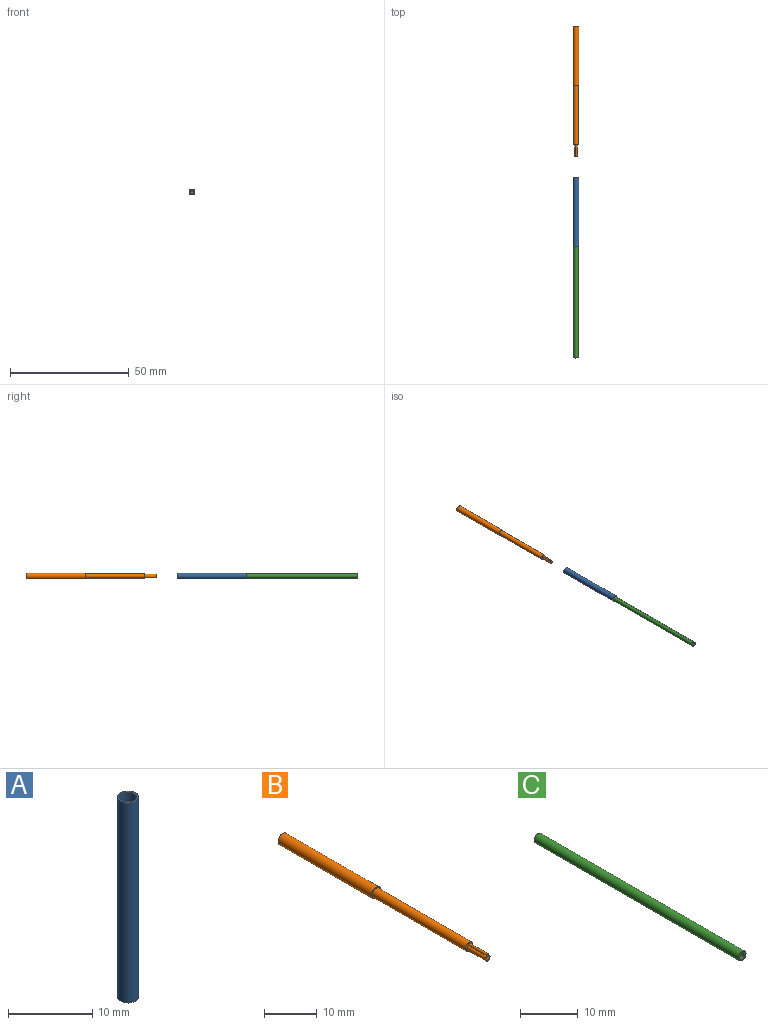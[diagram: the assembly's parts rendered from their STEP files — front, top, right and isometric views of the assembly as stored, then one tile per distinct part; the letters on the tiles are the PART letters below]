
ASSEMBLY  parts=3 mates=1
PART A: 4 faces, bbox 2.5x2.5x29 mm
  f0: cylinder r=1mm len=29mm, axis (0,0,-1), area 182.2mm2, adj f2,f3
  f1: cylinder r=1.25mm len=29mm, axis (0,0,-1), area 227.8mm2, adj f2,f3
  f2: plane 2.5x2.5mm, normal (0,0,1), area 1.8mm2, adj f0,f1
  f3: plane 2.5x2.5mm, normal (0,0,-1), area 1.8mm2, adj f0,f1
PART B: 8 faces, bbox 2.5x55x2.5 mm
  f0: cylinder r=0.6mm len=5mm, axis (0,1,0), area 17.1mm2, adj f1,f2,f4
  f1: cylinder r=0.25mm len=5mm, axis (0,1,0), area 5.9mm2, adj f0,f2,f4
  f2: plane 1.6x1.2mm, normal (0,-1,0), area 1.3mm2, adj f0,f1
  f3: cylinder r=1mm len=25mm, axis (0,-1,0), area 157.1mm2, adj f4,f7
  f4: plane 2x2mm, normal (0,-1,0), area 1.8mm2, adj f0,f1,f3
  f5: cylinder r=1.25mm len=25mm, axis (0,-1,0), area 196.3mm2, adj f6,f7
  f6: plane 2.5x2.5mm, normal (0,1,0), area 4.9mm2, adj f5
  f7: plane 2.5x2.5mm, normal (0,-1,0), area 1.8mm2, adj f3,f5
PART C: 5 faces, bbox 1.9x50x1.9 mm
  f0: cylinder r=0.25mm len=50mm, axis (0,1,0), area 58.9mm2, adj f1,f3,f4
  f1: cylinder r=0.6mm len=50mm, axis (0,1,0), area 170.5mm2, adj f0,f3,f4
  f2: cylinder r=0.95mm len=50mm, axis (0,1,0), area 298.5mm2, adj f3,f4
  f3: plane 1.9x1.9mm, normal (0,-1,0), area 1.5mm2, adj f0,f1,f2
  f4: plane 1.9x1.9mm, normal (0,1,0), area 1.5mm2, adj f0,f1,f2
PLACE A rot(axis=(0,0.71,-0.71),180deg) t=(4.94,50.84,-0.32)mm
PLACE B t=(4.94,64.57,-0.33)mm
PLACE C t=(4.94,24.92,-0.32)mm
MATE slider A.f1 <-> C.f2  axis (0,1,0) through (4.94,50.84,-0.32)mm
